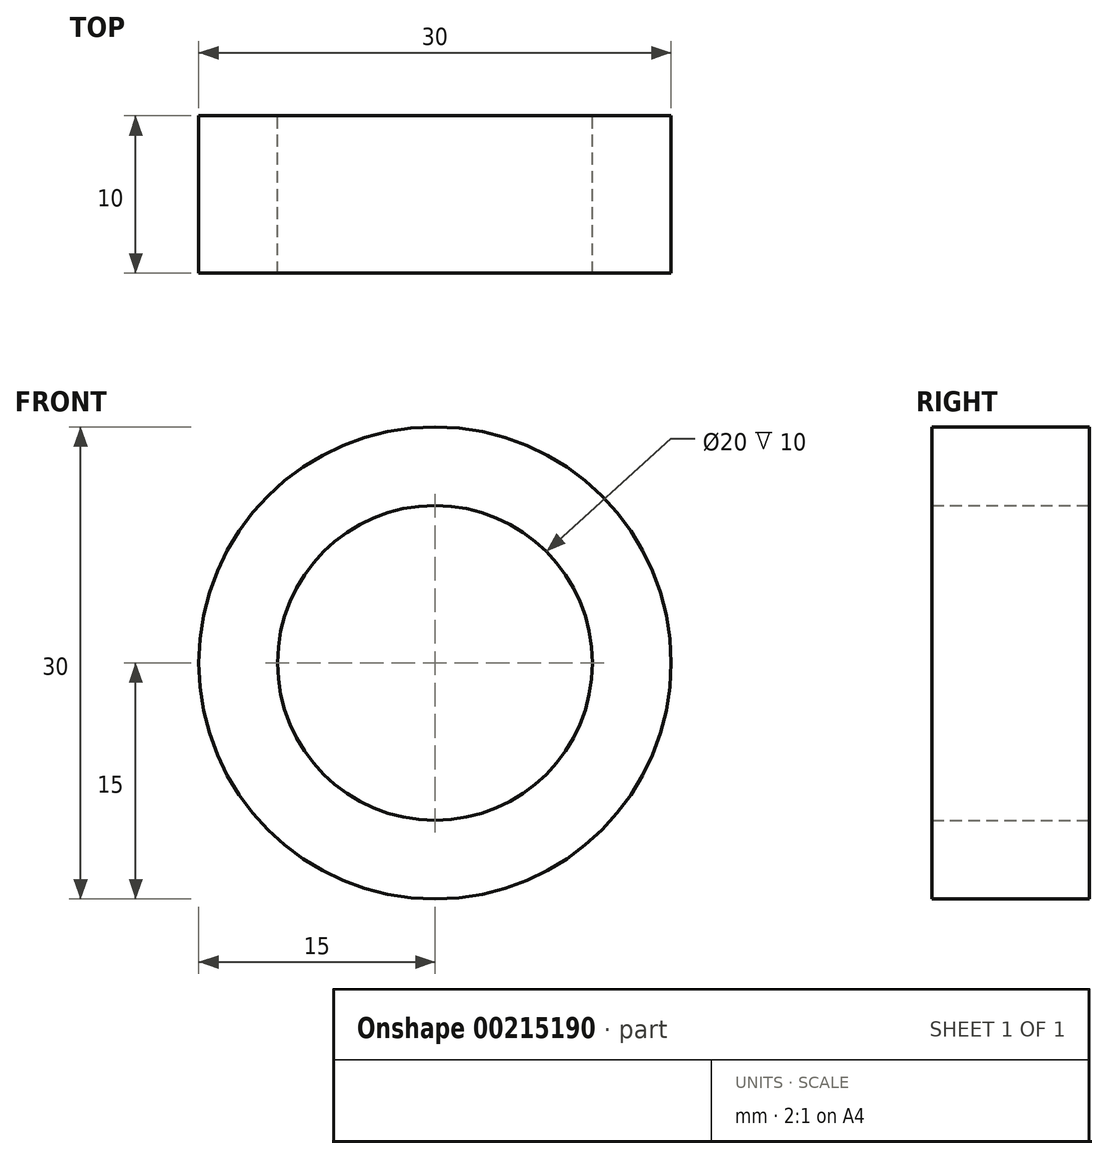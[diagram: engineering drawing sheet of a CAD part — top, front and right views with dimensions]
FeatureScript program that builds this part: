
annotation { "Feature Type Name" : "Feature", "Feature Type Description" : "" }
export const myFeature = defineFeature(function(context is Context, id is Id, definition is map)
    precondition{}
    {
        {
            var Q0;
            Q0=qCreatedBy(makeId("Front.planeOp"),FACE);
            var sketch = newSketch(context, id + "F0", { "sketchPlane" : qUnion([Q0])});
            skCircle(sketch, "E0", {"center": v(0, 0) * mm, "radius": 15 * mm});
            skCircle(sketch, "E1", {"center": v(0, 0) * mm, "radius": 10 * mm});
            skSolve(sketch);
        }
        {
            var Q0;
            Q0 = qSketchRegion(id + "F0", true);
            extrude(context, id + "F1", {"entities" : qUnion([Q0]), "depth" : 10 * mm});
        }
    });
